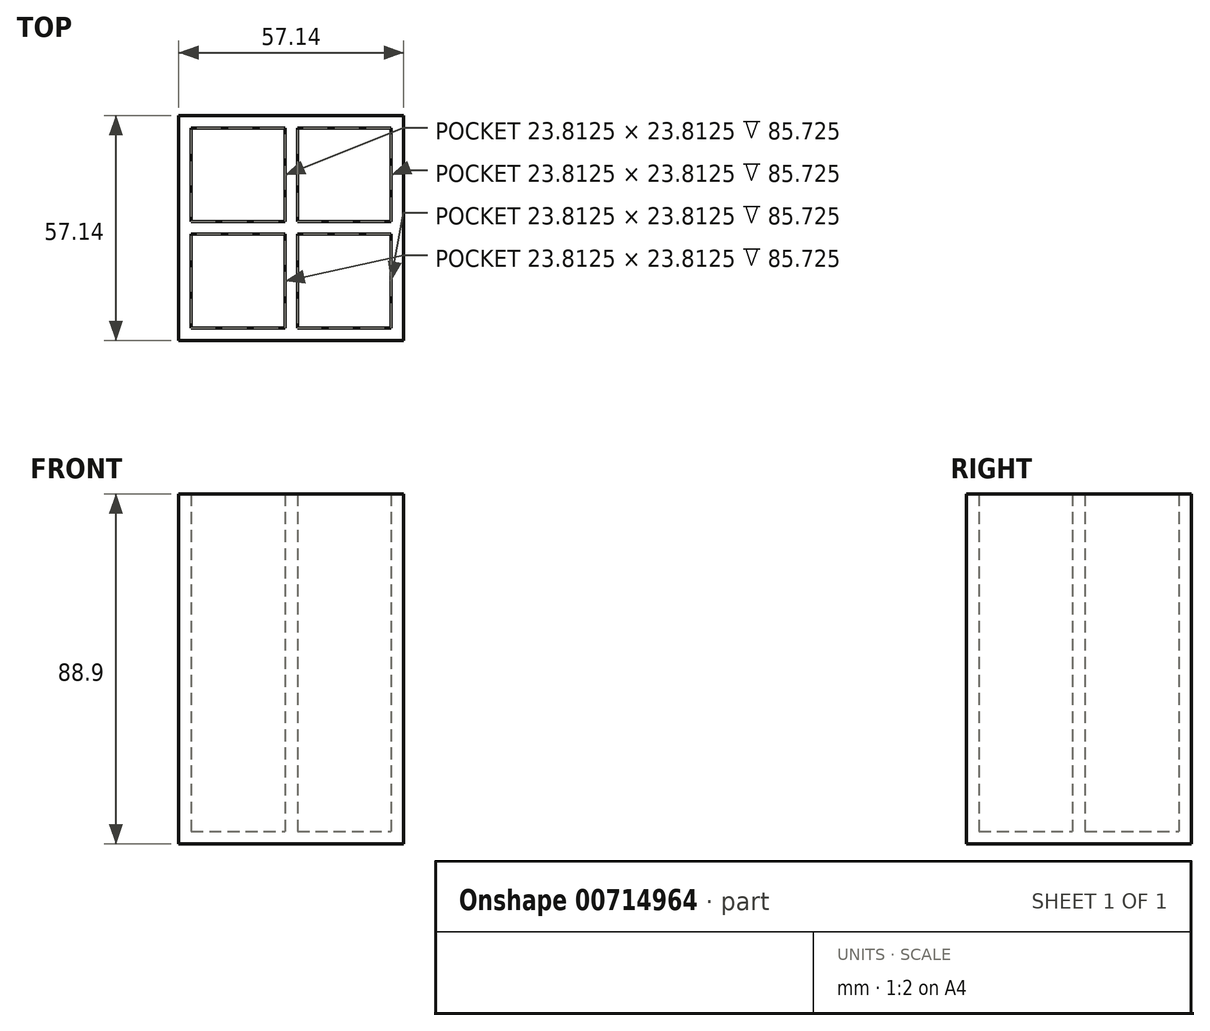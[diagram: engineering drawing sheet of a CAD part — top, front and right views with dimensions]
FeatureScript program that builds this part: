
annotation { "Feature Type Name" : "Feature", "Feature Type Description" : "" }
export const myFeature = defineFeature(function(context is Context, id is Id, definition is map)
    precondition{}
    {
        {
            var Q0;
            Q0=qCreatedBy(makeId("Top.planeOp"),FACE);
            var sketch = newSketch(context, id + "F0", { "sketchPlane" : qUnion([Q0])});
            skLineSegment(sketch, "E0.bottom", {"start": v(28.57, 28.58) * mm, "end": v(-28.58, 28.58) * mm});
            skLineSegment(sketch, "E0.top", {"start": v(28.57, -28.58) * mm, "end": v(-28.57, -28.58) * mm});
            skLineSegment(sketch, "E0.left", {"start": v(28.57, 28.58) * mm, "end": v(28.58, -28.57) * mm});
            skLineSegment(sketch, "E0.right", {"start": v(-28.58, 28.58) * mm, "end": v(-28.57, -28.57) * mm});
            skPoint(sketch, "E0.middle", {"position": v(0, 0) * mm});
            skSolve(sketch);
        }
        {
            var Q0;
            Q0=makeQuery(id+"F0.imprint","IMPRINT",FACE,{"disambiguationData":[TD([[makeQuery(id+"F0.imprint","IMPRINT",EDGE,{"derivedFrom":sQuery(id+"F0.wireOp",EDGE,"E0.bottom")}),1.0]])]});
            extrude(context, id + "F1", {"entities" : qUnion([Q0]), "depth" : 88.9 * mm});
        }
        {
            var Q0;
            Q0=makeQuery(id+"F1.opExtrude","CAP_FACE",FACE,{"disambiguationData":[OSD([sQuery(id+"F0.wireOp",EDGE,"E0.bottom"),sQuery(id+"F0.wireOp",EDGE,"E0.top"),sQuery(id+"F0.wireOp",EDGE,"E0.left"),sQuery(id+"F0.wireOp",EDGE,"E0.right")])],"isStart":true});
            var sketch = newSketch(context, id + "F2", { "sketchPlane" : qUnion([Q0])});
            skLineSegment(sketch, "E1.bottom", {"start": v(25.4, 25.4) * mm, "end": v(1.59, 25.4) * mm});
            skLineSegment(sketch, "E1.top", {"start": v(25.4, 1.59) * mm, "end": v(1.59, 1.59) * mm});
            skLineSegment(sketch, "E1.left", {"start": v(25.4, 25.4) * mm, "end": v(25.4, 1.59) * mm});
            skLineSegment(sketch, "E1.right", {"start": v(1.59, 25.4) * mm, "end": v(1.59, 1.59) * mm});
            skPoint(sketch, "E1.middle", {"position": v(13.5, 13.5) * mm});
            skLineSegment(sketch, "E2.bottom", {"start": v(25.4, -25.4) * mm, "end": v(1.59, -25.4) * mm});
            skLineSegment(sketch, "E2.top", {"start": v(25.4, -1.59) * mm, "end": v(1.59, -1.59) * mm});
            skLineSegment(sketch, "E2.left", {"start": v(25.4, -25.4) * mm, "end": v(25.4, -1.59) * mm});
            skLineSegment(sketch, "E2.right", {"start": v(1.59, -25.4) * mm, "end": v(1.59, -1.59) * mm});
            skPoint(sketch, "E2.middle", {"position": v(13.5, -13.5) * mm});
            skLineSegment(sketch, "E3.bottom", {"start": v(-1.59, -25.4) * mm, "end": v(-25.4, -25.4) * mm});
            skLineSegment(sketch, "E3.top", {"start": v(-1.59, -1.59) * mm, "end": v(-25.4, -1.59) * mm});
            skLineSegment(sketch, "E3.left", {"start": v(-1.59, -25.4) * mm, "end": v(-1.59, -1.59) * mm});
            skLineSegment(sketch, "E3.right", {"start": v(-25.4, -25.4) * mm, "end": v(-25.4, -1.59) * mm});
            skPoint(sketch, "E3.middle", {"position": v(-13.5, -13.5) * mm});
            skLineSegment(sketch, "E4.bottom", {"start": v(-1.59, 1.59) * mm, "end": v(-25.4, 1.59) * mm});
            skLineSegment(sketch, "E4.top", {"start": v(-1.59, 25.4) * mm, "end": v(-25.4, 25.4) * mm});
            skLineSegment(sketch, "E4.left", {"start": v(-1.59, 1.59) * mm, "end": v(-1.59, 25.4) * mm});
            skLineSegment(sketch, "E4.right", {"start": v(-25.4, 1.59) * mm, "end": v(-25.4, 25.4) * mm});
            skPoint(sketch, "E4.middle", {"position": v(-13.5, 13.5) * mm});
            skSolve(sketch);
        }
        {
            var Q0;
            Q0=makeQuery(id+"F2.imprint","IMPRINT",FACE,{"disambiguationData":[TD([[makeQuery(id+"F2.imprint","IMPRINT",EDGE,{"derivedFrom":sQuery(id+"F2.wireOp",EDGE,"E4.bottom")}),-1.0]])]});
            var Q1;
            Q1=makeQuery(id+"F2.imprint","IMPRINT",FACE,{"disambiguationData":[TD([[makeQuery(id+"F2.imprint","IMPRINT",EDGE,{"derivedFrom":sQuery(id+"F2.wireOp",EDGE,"E1.bottom")}),1.0]])]});
            var Q2;
            Q2=makeQuery(id+"F2.imprint","IMPRINT",FACE,{"disambiguationData":[TD([[makeQuery(id+"F2.imprint","IMPRINT",EDGE,{"derivedFrom":sQuery(id+"F2.wireOp",EDGE,"E2.bottom")}),-1.0]])]});
            var Q3;
            Q3=makeQuery(id+"F2.imprint","IMPRINT",FACE,{"disambiguationData":[TD([[makeQuery(id+"F2.imprint","IMPRINT",EDGE,{"derivedFrom":sQuery(id+"F2.wireOp",EDGE,"E3.bottom")}),-1.0]])]});
            extrude(context, id + "F3", {"entities" : qUnion([Q0, Q1, Q2, Q3]), "operationType" : NewBodyOperationType.REMOVE, "oppositeDirection" : true, "depth" : 111.25 * mm});
        }
        {
            var Q0;
            Q0=makeQuery(id+"F1.opExtrude","CAP_FACE",FACE,{"disambiguationData":[OSD([sQuery(id+"F0.wireOp",EDGE,"E0.bottom"),sQuery(id+"F0.wireOp",EDGE,"E0.top"),sQuery(id+"F0.wireOp",EDGE,"E0.left"),sQuery(id+"F0.wireOp",EDGE,"E0.right")])],"isStart":true});
            var sketch = newSketch(context, id + "F4", { "sketchPlane" : qUnion([Q0])});
            skLineSegment(sketch, "E5.bottom", {"start": v(-28.57, 28.57) * mm, "end": v(28.57, 28.57) * mm});
            skLineSegment(sketch, "E5.top", {"start": v(-28.57, -28.58) * mm, "end": v(28.57, -28.58) * mm});
            skLineSegment(sketch, "E5.left", {"start": v(-28.57, 28.57) * mm, "end": v(-28.57, -28.58) * mm});
            skLineSegment(sketch, "E5.right", {"start": v(28.57, 28.57) * mm, "end": v(28.57, -28.58) * mm});
            skSolve(sketch);
        }
        {
            var Q0;
            Q0=qSketchRegion(id+"F4",true);
            extrude(context, id + "F5", {"entities" : qUnion([Q0]), "operationType" : NewBodyOperationType.ADD, "oppositeDirection" : true, "depth" : 3.17 * mm});
        }
    });
